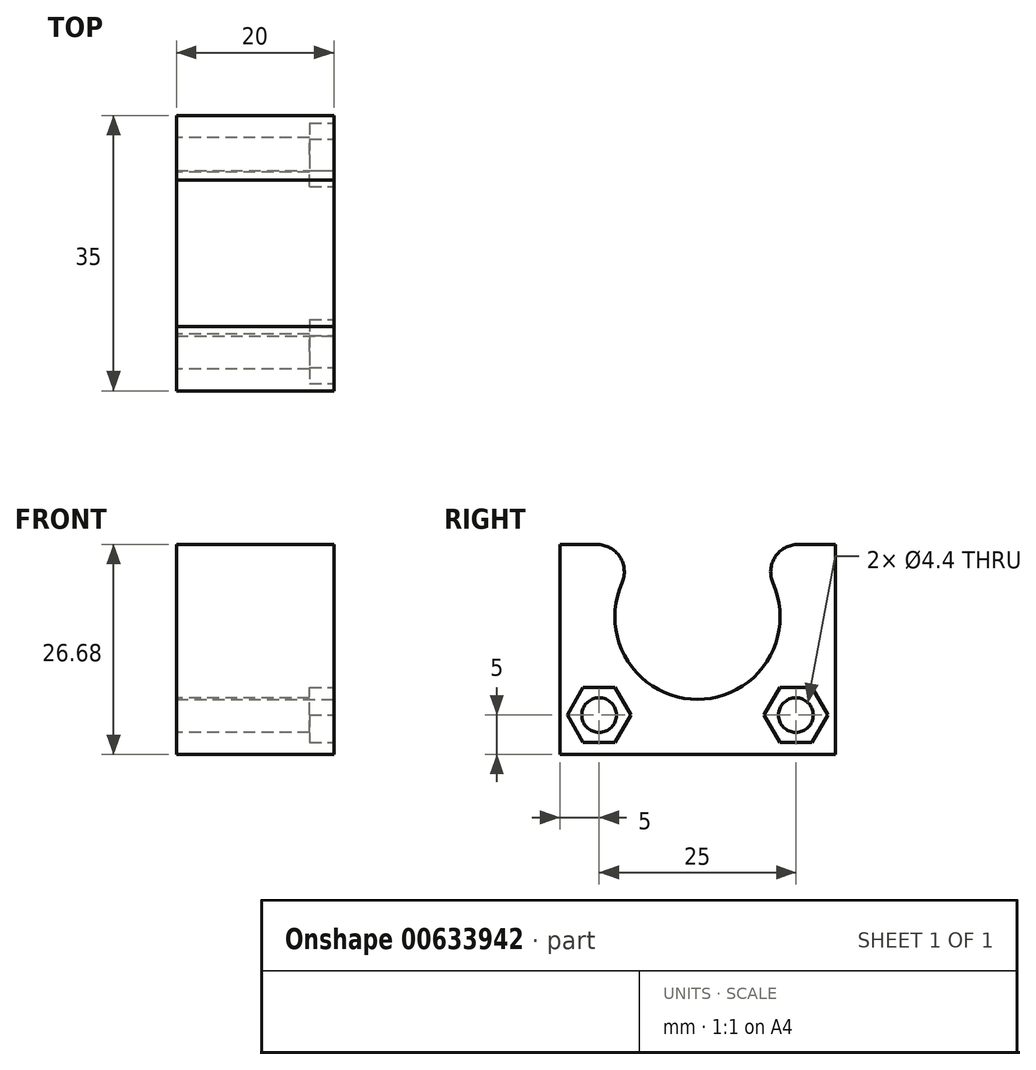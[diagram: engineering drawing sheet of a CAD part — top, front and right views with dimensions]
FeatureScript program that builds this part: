
annotation { "Feature Type Name" : "Feature", "Feature Type Description" : "" }
export const myFeature = defineFeature(function(context is Context, id is Id, definition is map)
    precondition{}
    {
        {
            var Q0;
            Q0=qCreatedBy(makeId("Right.planeOp"),FACE);
            var sketch = newSketch(context, id + "F0", { "sketchPlane" : qUnion([Q0])});
            skLineSegment(sketch, "E0.bottom", {"start": v(-17.5, -17.5) * mm, "end": v(17.5, -17.5) * mm});
            skLineSegment(sketch, "E0.top", {"start": v(-17.5, 17.5) * mm, "end": v(17.5, 17.5) * mm});
            skLineSegment(sketch, "E0.left", {"start": v(-17.5, -17.5) * mm, "end": v(-17.5, 17.5) * mm});
            skLineSegment(sketch, "E0.right", {"start": v(17.5, -17.5) * mm, "end": v(17.5, 17.5) * mm});
            skPoint(sketch, "E0.middle", {"position": v(0, 0) * mm});
            skSolve(sketch);
        }
        {
            var Q0;
            Q0 = qSketchRegion(id + "F0", true);
            extrude(context, id + "F1", {"entities" : qUnion([Q0]), "depth" : 20 * mm, "offsetDistance" : 25 * mm});
        }
        {
            var Q0;
            Q0=makeQuery(id+"F1.opExtrude","CAP_FACE",FACE,{"disambiguationData":[OSD([sQuery(id+"F0.wireOp",EDGE,"E0.bottom"),sQuery(id+"F0.wireOp",EDGE,"E0.top"),sQuery(id+"F0.wireOp",EDGE,"E0.left"),sQuery(id+"F0.wireOp",EDGE,"E0.right")])],"isStart":false});
            var sketch = newSketch(context, id + "F2", { "sketchPlane" : qUnion([Q0])});
            skCircle(sketch, "E1", {"center": v(0, 0) * mm, "radius": 10.5 * mm});
            skLineSegment(sketch, "E2", {"start": v(-5.1, 9.18) * mm, "end": v(-17.5, 9.18) * mm});
            skLineSegment(sketch, "E3", {"start": v(-17.5, 9.18) * mm, "end": v(-5.1, 9.18) * mm});
            skLineSegment(sketch, "E4.trimOffspring", {"start": v(5.1, 9.18) * mm, "end": v(17.5, 9.18) * mm});
            skLineSegment(sketch, "E5", {"start": v(-17.5, 9.18) * mm, "end": v(-17.5, 17.5) * mm});
            skLineSegment(sketch, "E6", {"start": v(-17.5, 17.5) * mm, "end": v(17.5, 17.5) * mm});
            skLineSegment(sketch, "E7", {"start": v(17.5, 17.5) * mm, "end": v(17.5, 9.18) * mm});
            skSolve(sketch);
        }
        {
            var Q0;
            Q0 = qSketchRegion(id + "F2", true);
            extrude(context, id + "F3", {"entities" : qUnion([Q0]), "operationType" : NewBodyOperationType.REMOVE, "oppositeDirection" : true, "depth" : 51.1 * mm, "offsetDistance" : 25 * mm});
        }
        {
            var Q0;
            Q0=makeQuery(id+"F3.boolean.opBoolean","COPY",EDGE,{"derivedFrom":makeQuery(id+"F3.opExtrude","SWEPT_EDGE",EDGE,{"disambiguationData":[OSD([sQuery(id+"F2.wireOp",EDGE,"E1"),sQuery(id+"F2.wireOp",EDGE,"E4.trimOffspring")])]})});
            var Q1;
            Q1=makeQuery(id+"F3.boolean.opBoolean","COPY",EDGE,{"derivedFrom":makeQuery(id+"F3.opExtrude","SWEPT_EDGE",EDGE,{"disambiguationData":[OSD([sQuery(id+"F2.wireOp",EDGE,"E1"),sQuery(id+"F2.wireOp",EDGE,"E3")])]})});
            fillet(context, id + "F4", {"entities" : qUnion([Q0, Q1]), "radius" : 3.5 * mm, "tangentPropagation" : true, "allowEdgeOverflow" : false});
        }
        {
            var Q0;
            Q0=makeQuery(id+"F1.opExtrude","CAP_FACE",FACE,{"disambiguationData":[OSD([sQuery(id+"F0.wireOp",EDGE,"E0.bottom"),sQuery(id+"F0.wireOp",EDGE,"E0.top"),sQuery(id+"F0.wireOp",EDGE,"E0.left"),sQuery(id+"F0.wireOp",EDGE,"E0.right")])],"isStart":false});
            var sketch = newSketch(context, id + "F5", { "sketchPlane" : qUnion([Q0])});
            skPoint(sketch, "E8.startSnap0", {"position": v(15.15, 9.18) * mm});
            skPoint(sketch, "E9.orphan", {"position": v(0, -14) * mm});
            skPoint(sketch, "E10.orphan", {"position": v(0, -10.5) * mm});
            skPoint(sketch, "E11.end.orphan", {"position": v(0, -17.5) * mm});
            skPoint(sketch, "E12.orphan", {"position": v(-15.15, 9.18) * mm});
            skPoint(sketch, "E8.end.orphan", {"position": v(15.15, 9.18) * mm});
            skPoint(sketch, "E13.center.orphan", {"position": v(15.15, -10.82) * mm});
            skPoint(sketch, "E14.center.orphan", {"position": v(-11.5, -11.17) * mm});
            skLineSegment(sketch, "E15", {"start": v(17.5, -12.5) * mm, "end": v(16.54, -12.5) * mm, "construction": true});
            skCircle(sketch, "E16.cCircle", {"center": v(12.5, -12.5) * mm, "radius": 3.5 * mm, "construction": true});
            skLineSegment(sketch, "E16.0", {"start": v(14.52, -16) * mm, "end": v(10.48, -16) * mm});
            skLineSegment(sketch, "E16.1", {"start": v(10.48, -16) * mm, "end": v(8.46, -12.5) * mm});
            skLineSegment(sketch, "E16.2", {"start": v(8.46, -12.5) * mm, "end": v(10.48, -9) * mm});
            skLineSegment(sketch, "E16.3", {"start": v(10.48, -9) * mm, "end": v(14.52, -9) * mm});
            skLineSegment(sketch, "E16.4", {"start": v(14.52, -9) * mm, "end": v(16.54, -12.5) * mm});
            skLineSegment(sketch, "E16.5", {"start": v(16.54, -12.5) * mm, "end": v(14.52, -16) * mm});
            skPoint(sketch, "E16.0.midPoint", {"position": v(12.5, -16) * mm});
            skPoint(sketch, "E17.orphan", {"position": v(8.26, -12.5) * mm});
            skPoint(sketch, "E18.start.orphan", {"position": v(8.26, -17.5) * mm});
            skLineSegment(sketch, "E19", {"start": v(0, -10.5) * mm, "end": v(0, -17.5) * mm});
            skLineSegment(sketch, "E20.MirrorCS", {"start": v(-10.48, -9) * mm, "end": v(-14.52, -9) * mm});
            skLineSegment(sketch, "E21.MirrorCS", {"start": v(-14.52, -9) * mm, "end": v(-16.54, -12.5) * mm});
            skLineSegment(sketch, "E22.MirrorCS", {"start": v(-16.54, -12.5) * mm, "end": v(-14.52, -16) * mm});
            skLineSegment(sketch, "E23.MirrorCS", {"start": v(-14.52, -16) * mm, "end": v(-10.48, -16) * mm});
            skLineSegment(sketch, "E24.MirrorCS", {"start": v(-10.48, -16) * mm, "end": v(-8.46, -12.5) * mm});
            skLineSegment(sketch, "E25.MirrorCS", {"start": v(-8.46, -12.5) * mm, "end": v(-10.48, -9) * mm});
            skCircle(sketch, "E26.MirrorC", {"center": v(-12.5, -12.5) * mm, "radius": 3.5 * mm, "construction": true});
            skSolve(sketch);
        }
        {
            var Q0;
            Q0 = qSketchRegion(id + "F5", true);
            extrude(context, id + "F6", {"entities" : qUnion([Q0]), "operationType" : NewBodyOperationType.REMOVE, "oppositeDirection" : true, "depth" : 3.1 * mm, "offsetDistance" : 25 * mm});
        }
        {
            var Q0;
            Q0=makeQuery(id+"F1.opExtrude","CAP_FACE",FACE,{"disambiguationData":[OSD([sQuery(id+"F0.wireOp",EDGE,"E0.bottom"),sQuery(id+"F0.wireOp",EDGE,"E0.top"),sQuery(id+"F0.wireOp",EDGE,"E0.left"),sQuery(id+"F0.wireOp",EDGE,"E0.right")])],"isStart":true});
            var sketch = newSketch(context, id + "F7", { "sketchPlane" : qUnion([Q0])});
            skLineSegment(sketch, "E27", {"start": v(-17.5, -12.5) * mm, "end": v(-12.5, -12.5) * mm, "construction": true});
            skPoint(sketch, "E28.end.orphan", {"position": v(-9.14, -12.5) * mm});
            skPoint(sketch, "E28.start.orphan", {"position": v(-9.14, -17.5) * mm});
            skCircle(sketch, "E29", {"center": v(-12.5, -12.5) * mm, "radius": 2.3 * mm});
            skLineSegment(sketch, "E30", {"start": v(0, -10.5) * mm, "end": v(0, -17.5) * mm, "construction": true});
            skCircle(sketch, "E31.MirrorC", {"center": v(12.5, -12.5) * mm, "radius": 2.3 * mm});
            skSolve(sketch);
        }
        {
            var Q0;
            Q0=sQuery(id+"F7.wireOp",VERTEX,"E27.end");
            var Q1;
            Q1=sQuery(id+"F7.wireOp",VERTEX,"E31.MirrorC.center");
            var Q2;
            Q2=makeQuery(id+"F1.opExtrude","SWEPT_BODY",BODY,{"disambiguationData":[OSD([sQuery(id+"F0.wireOp",EDGE,"E0.bottom"),sQuery(id+"F0.wireOp",EDGE,"E0.top"),sQuery(id+"F0.wireOp",EDGE,"E0.left"),sQuery(id+"F0.wireOp",EDGE,"E0.right")])]});
            hole(context, id + "F8", {"style" : HoleStyle.SIMPLE, "endStyle" : HoleEndStyle.THROUGH, "holeDiameter" : 4.4 * mm, "majorDiameter" : 5 * mm, "isTappedThrough" : true, "tappedDepth" : 12 * mm, "tapClearance" : 3, "locations" : qUnion([Q0, Q1]), "scope" : qUnion([Q2])});
        }
    });
